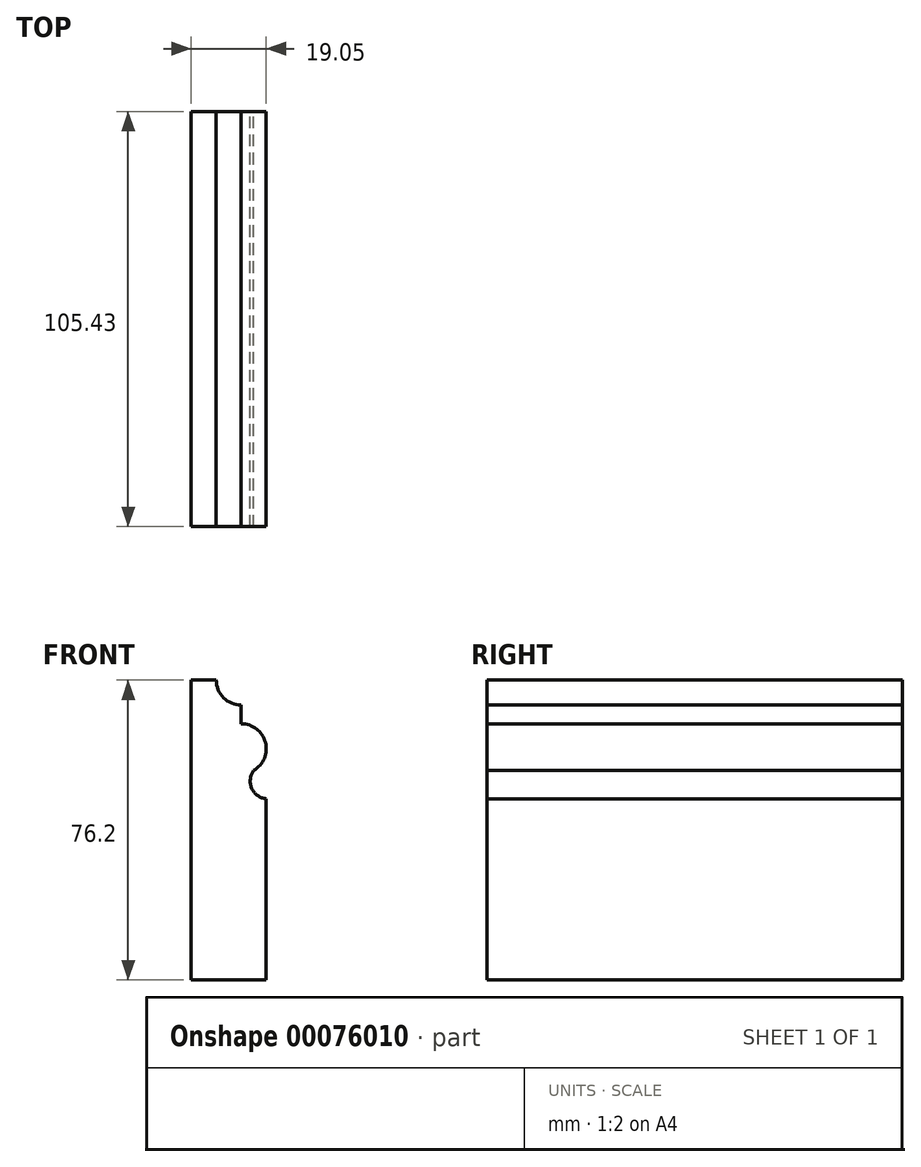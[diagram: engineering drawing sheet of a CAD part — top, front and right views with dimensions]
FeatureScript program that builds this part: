
annotation { "Feature Type Name" : "Feature", "Feature Type Description" : "" }
export const myFeature = defineFeature(function(context is Context, id is Id, definition is map)
    precondition{}
    {
        {
            var Q0;
            Q0=qCreatedBy(makeId("Front.planeOp"),FACE);
            var sketch = newSketch(context, id + "F0", { "sketchPlane" : qUnion([Q0])});
            skLineSegment(sketch, "E0", {"start": v(-3.41, 47.78) * mm, "end": v(2.94, 47.78) * mm});
            skLineSegment(sketch, "E1", {"start": v(-3.41, 47.78) * mm, "end": v(-3.41, -28.42) * mm});
            skLineSegment(sketch, "E2", {"start": v(-3.41, -28.42) * mm, "end": v(15.64, -28.42) * mm});
            skLineSegment(sketch, "E3", {"start": v(9.29, 41.43) * mm, "end": v(9.29, 36.67) * mm});
            skLineSegment(sketch, "E4", {"start": v(15.64, 17.62) * mm, "end": v(15.64, -28.42) * mm});
            skArc(sketch, "E5", {"start": v(2.94, 47.78) * mm, "mid": v(4.8, 43.3) * mm, "end": v(9.29, 41.43) * mm});
            skArc(sketch, "E6", {"start": v(15.64, 30.32) * mm, "mid": v(13.78, 34.8) * mm, "end": v(9.29, 36.67) * mm});
            skArc(sketch, "E7", {"start": v(12.46, 24.82) * mm, "mid": v(14.79, 27.14) * mm, "end": v(15.64, 30.32) * mm});
            skArc(sketch, "E8", {"start": v(12.46, 24.82) * mm, "mid": v(11.94, 20.29) * mm, "end": v(15.64, 17.62) * mm});
            skSolve(sketch);
        }
        {
            var Q0;
            Q0=sQuery(id+"F0.wireOp",EDGE,"E8");
            var Q1;
            Q1=sQuery(id+"F0.wireOp",EDGE,"E2");
            var Q2;
            Q2=sQuery(id+"F0.wireOp",EDGE,"E1");
            var Q3;
            Q3=sQuery(id+"F0.wireOp",EDGE,"E6");
            var Q4;
            Q4=sQuery(id+"F0.wireOp",EDGE,"E5");
            var Q5;
            Q5=sQuery(id+"F0.wireOp",EDGE,"E4");
            var Q6;
            Q6=sQuery(id+"F0.wireOp",EDGE,"E0");
            var Q7;
            Q7=sQuery(id+"F0.wireOp",EDGE,"E3");
            var Q8;
            Q8=sQuery(id+"F0.wireOp",EDGE,"E7");
            extrude(context, id + "F1", {"bodyType" : ToolBodyType.SURFACE, "surfaceEntities" : qUnion([Q0, Q1, Q2, Q3, Q4, Q5, Q6, Q7, Q8]), "oppositeDirection" : true, "depth" : 105.43 * mm});
        }
    });
